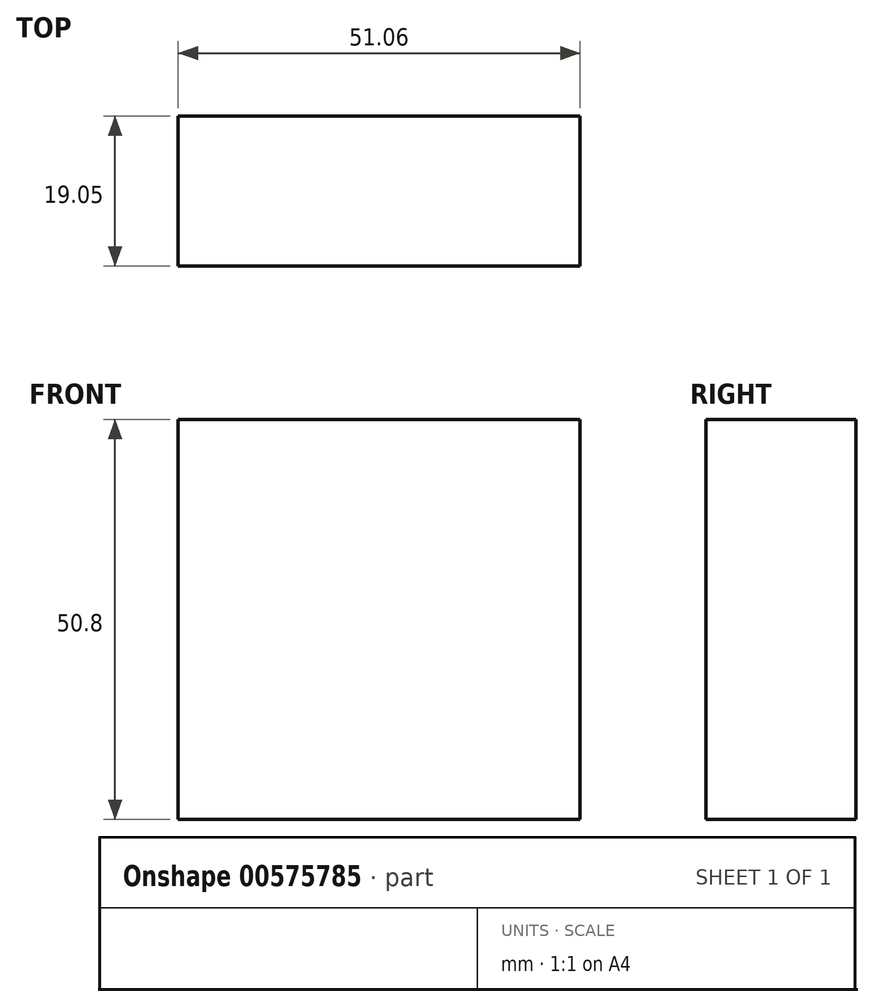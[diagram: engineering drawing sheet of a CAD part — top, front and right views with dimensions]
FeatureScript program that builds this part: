
annotation { "Feature Type Name" : "Feature", "Feature Type Description" : "" }
export const myFeature = defineFeature(function(context is Context, id is Id, definition is map)
    precondition{}
    {
        {
            var Q0;
            Q0=qCreatedBy(makeId("Front.planeOp"),FACE);
            var sketch = newSketch(context, id + "F0", { "sketchPlane" : qUnion([Q0])});
            skLineSegment(sketch, "E0.bottom", {"start": v(-25.53, 25.4) * mm, "end": v(25.53, 25.4) * mm});
            skLineSegment(sketch, "E0.top", {"start": v(-25.53, -25.4) * mm, "end": v(25.53, -25.4) * mm});
            skLineSegment(sketch, "E0.left", {"start": v(-25.53, 25.4) * mm, "end": v(-25.53, -25.4) * mm});
            skLineSegment(sketch, "E0.right", {"start": v(25.53, 25.4) * mm, "end": v(25.53, -25.4) * mm});
            skPoint(sketch, "E0.middle", {"position": v(0, 0) * mm});
            skSolve(sketch);
        }
        {
            var Q0;
            Q0 = qSketchRegion(id + "F0", true);
            extrude(context, id + "F1", {"entities" : qUnion([Q0]), "depth" : 19.05 * mm, "offsetDistance" : 25.4 * mm});
        }
    });
